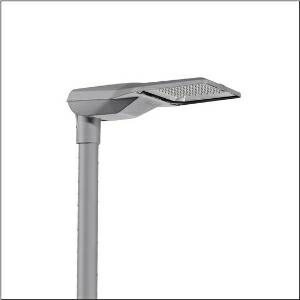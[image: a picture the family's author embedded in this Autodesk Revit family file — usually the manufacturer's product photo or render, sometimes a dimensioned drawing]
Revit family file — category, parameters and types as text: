
# Revit family: streetlight_sl_21_iq_midi___st1_0a_5xe3d31d08mb_825e
name_source: partatom
category: Lighting Fixtures
units: mm (PartAtom-declared; Revit-internal decimal feet)

## family parameters
Cut with Voids When Loaded = No
Host = Face
Light Source = No
Part Type = Normal
Room Calculation Point = No
Round Connector Dimension = Use Diameter
Shared = No

## types (1)
- --- (1 x LED, 19500 lm, 146.7 W, 3000K)
    Apparent Load = 147 VA
    CIE Flux Codes = 37 72 97 100 100
    Color Rendering = 70
    Color Temperature = 3000K
    Default Elevation = 1800 mm
    Description = Streetlight SL 21 iQ midi, mast luminaire, primary light control with lens, of PMMA, primary optical cover: cover, of toughened safety glass, transparent, light distribution: ST1.0a, light emission: direct distribution, primary light characteristic: asymmetric, installation type: post-top, side-entry, LED, High Power LED, rated luminous flux: 19.500lm, luminous efficacy: 133lm/W, light colour: 730, colour temperature: 3000K, control gear: iQ-Comfort, control: Auto-Match, Temp-Guard, Lumen-Switch, Night-Set, Smart-Wire, Light-Fading, Desk-Remote (wireless, voltage-free reading and setting of iQ features in the workshop via application-optimized NFC function/RFID function), optimised constant luminous flux control (CLO 2.0), pre-setting: linear dimming characteristic, mains connection: 230..240V, AC, 50/60Hz, start of lifetime: 147W, end of service life: 161W, reduction: 62W, luminaire housing, of diecast aluminium, powder-coated, Siteco® metallic grey (DB 702S), corrosivity category C5 mid according to DIN EN ISO 12944, please order mast flange separately, inclination adjustable: 0°, 5°, 10°, 15°, sealing non-destructively replaceable, multi-level sealing system, length: 644mm, width: 335mm, height: 110mm, mast flange for spigot size: 42mm (side-entry): 5XC10008XM4, 60/48mm (side-entry/post-top): 5XC10108XM2, 76/60mm (side-entry/post-top): 5XC10108XM1, mounting height: 4..8m, protection rating (complete): IP66, insulation class (complete): insulation class II (safety insulation), certification: CE, ENEC, ENEC+, VDE, impact resistance: IK10, permissible operating ambient temperature for outdoor applications: -40..+50°C, standard-compliant lighting for roads and squares, packaging unit: 1 piece

Light Distribution: ST1.0a
    Height = 111 mm
    Lamp = 1 x LED
    Lamp Light Flux = 19500 lm
    Lamp Power = 146.7 W
    Lamp count = 1
    Length = 644 mm
    Luminous efficacy = 133 lm/W
    Manufacturer = Siteco
    ModVariant = No
    Model = 5XE3D31D08MB
    Number of Poles = 1
    OnlyDefault = Yes
    Power Factor = 1
    Product Name = Streetlight SL 21 iQ midi | ST1.0a
    Product group = mast luminaire | pylon top
    ProductGroupID = 6100
    Protection Class = Protection class II
    Protection Degree = IP 66
    RLX_Detail_Level = 1
    RLX_Emergency_Light_Flux = 0 lm
    RLX_Emergency_Type = 0
    RLX_Emergency_Type_DB = No
    RlxData = <blob elided: 26885 chars, md5=7041228a>
    Socket = socket
    Standby Power = 0 W
    System Light Flux = 19499 lm
    System Power = 147 W
    Type Comments = factory setting: luminous flux: 100 % | dim-lin: 254 | 753 mA
    Type Image = l_1004298.jpg
    URL = http://relux.com
    VarID = @adj_210833
    Voltage = 0 V
    Weight = 0.00 kg
    Width = 336 mm

## geometry (parser evidence)
native form markers: Blend x4, Sweep x9
no freeform markers — native parametric forms only
